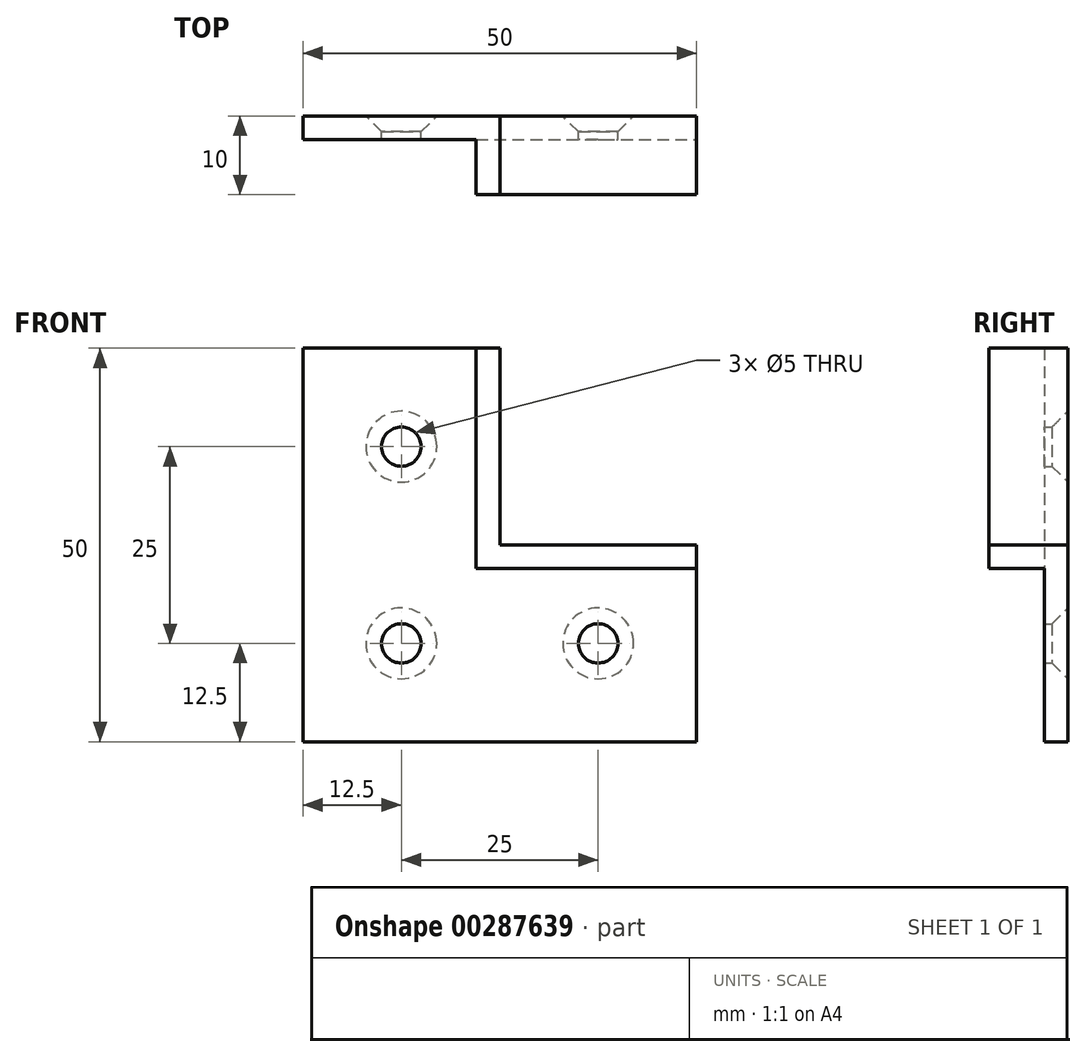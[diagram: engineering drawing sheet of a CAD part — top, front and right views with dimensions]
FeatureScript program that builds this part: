
annotation { "Feature Type Name" : "Feature", "Feature Type Description" : "" }
export const myFeature = defineFeature(function(context is Context, id is Id, definition is map)
    precondition{}
    {
        {
            var Q0;
            Q0=qCreatedBy(makeId("Front.planeOp"),FACE);
            var sketch = newSketch(context, id + "F0", { "sketchPlane" : qUnion([Q0])});
            skLineSegment(sketch, "E0", {"start": v(0, 0) * mm, "end": v(-25, 0) * mm});
            skLineSegment(sketch, "E1", {"start": v(-25, 0) * mm, "end": v(-25, -50) * mm});
            skLineSegment(sketch, "E2", {"start": v(-25, -50) * mm, "end": v(25, -50) * mm});
            skLineSegment(sketch, "E3", {"start": v(25, -50) * mm, "end": v(25, -25) * mm});
            skLineSegment(sketch, "E4", {"start": v(25, -25) * mm, "end": v(0, -25) * mm});
            skLineSegment(sketch, "E5", {"start": v(0, -25) * mm, "end": v(0, 0) * mm});
            skSolve(sketch);
        }
        {
            var Q0;
            Q0=makeQuery(id+"F0.imprint","IMPRINT",FACE,{"disambiguationData":[TD([[makeQuery(id+"F0.imprint","IMPRINT",EDGE,{"derivedFrom":sQuery(id+"F0.wireOp",EDGE,"E0")}),1.0]])]});
            extrude(context, id + "F1", {"entities" : qUnion([Q0]), "oppositeDirection" : true, "depth" : 3 * mm});
        }
        {
            var Q0;
            Q0=makeQuery(id+"F1.opExtrude","CAP_FACE",FACE,{"disambiguationData":[OSD([sQuery(id+"F0.wireOp",EDGE,"E0"),sQuery(id+"F0.wireOp",EDGE,"E1"),sQuery(id+"F0.wireOp",EDGE,"E2"),sQuery(id+"F0.wireOp",EDGE,"E3"),sQuery(id+"F0.wireOp",EDGE,"E4"),sQuery(id+"F0.wireOp",EDGE,"E5")])],"isStart":true});
            var sketch = newSketch(context, id + "F2", { "sketchPlane" : qUnion([Q0])});
            skLineSegment(sketch, "E6", {"start": v(0, 0) * mm, "end": v(-3, 0) * mm});
            skLineSegment(sketch, "E7", {"start": v(-3, 0) * mm, "end": v(-3, -28) * mm});
            skLineSegment(sketch, "E8", {"start": v(-3, -28) * mm, "end": v(25, -28) * mm});
            skLineSegment(sketch, "E9", {"start": v(25, -28) * mm, "end": v(25, -25) * mm});
            skLineSegment(sketch, "E10", {"start": v(25, -25) * mm, "end": v(0, -25) * mm});
            skLineSegment(sketch, "E11", {"start": v(0, -25) * mm, "end": v(0, 0) * mm});
            skSolve(sketch);
        }
        {
            var Q0;
            Q0=makeQuery(id+"F2.imprint","IMPRINT",FACE,{"disambiguationData":[TD([[makeQuery(id+"F2.imprint","IMPRINT",EDGE,{"derivedFrom":sQuery(id+"F2.wireOp",EDGE,"E6")}),1.0]])]});
            extrude(context, id + "F3", {"entities" : qUnion([Q0]), "operationType" : NewBodyOperationType.ADD, "depth" : 7 * mm});
        }
        {
            var Q0;
            Q0=makeQuery(id+"F1.opExtrude","CAP_FACE",FACE,{"disambiguationData":[OSD([sQuery(id+"F0.wireOp",EDGE,"E0"),sQuery(id+"F0.wireOp",EDGE,"E1"),sQuery(id+"F0.wireOp",EDGE,"E2"),sQuery(id+"F0.wireOp",EDGE,"E3"),sQuery(id+"F0.wireOp",EDGE,"E4"),sQuery(id+"F0.wireOp",EDGE,"E5")])],"isStart":false});
            var sketch = newSketch(context, id + "F4", { "sketchPlane" : qUnion([Q0])});
            skLineSegment(sketch, "E12.0", {"start": v(-7.22, -12.5) * mm, "end": v(30.88, -12.5) * mm});
            skLineSegment(sketch, "E13.0", {"start": v(12.5, 5.6) * mm, "end": v(12.5, -54.93) * mm});
            skLineSegment(sketch, "E14.0", {"start": v(-30.82, -37.5) * mm, "end": v(33.81, -37.5) * mm});
            skLineSegment(sketch, "E15.0", {"start": v(-12.5, -22.4) * mm, "end": v(-12.5, -54.78) * mm});
            skPoint(sketch, "E16", {"position": v(12.5, -12.5) * mm});
            skPoint(sketch, "E17", {"position": v(12.5, -37.5) * mm});
            skPoint(sketch, "E18", {"position": v(-12.5, -37.5) * mm});
            skSolve(sketch);
        }
        {
            var Q0;
            Q0=sQuery(id+"F4.wireOp",VERTEX,"E16");
            var Q1;
            Q1=sQuery(id+"F4.wireOp",VERTEX,"E17");
            var Q2;
            Q2=sQuery(id+"F4.wireOp",VERTEX,"E18");
            var Q3;
            Q3=makeQuery(id+"F1.opExtrude","SWEPT_BODY",BODY,{"disambiguationData":[OSD([sQuery(id+"F0.wireOp",EDGE,"E0"),sQuery(id+"F0.wireOp",EDGE,"E1"),sQuery(id+"F0.wireOp",EDGE,"E2"),sQuery(id+"F0.wireOp",EDGE,"E3"),sQuery(id+"F0.wireOp",EDGE,"E4"),sQuery(id+"F0.wireOp",EDGE,"E5")])]});
            hole(context, id + "F5", {"style" : HoleStyle.C_SINK, "endStyle" : HoleEndStyle.THROUGH, "holeDiameter" : 5 * mm, "cSinkDiameter" : 9 * mm, "cSinkAngle" : 90 * degree, "tappedDepth" : 12 * mm, "tapClearance" : 3, "startFromSketch" : true, "locations" : qUnion([Q0, Q1, Q2]), "scope" : qUnion([Q3])});
        }
    });
